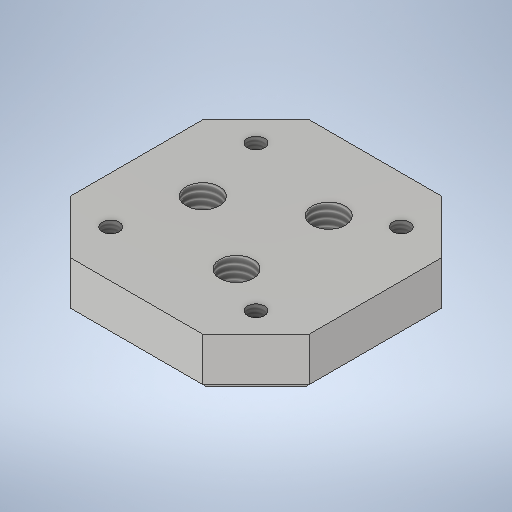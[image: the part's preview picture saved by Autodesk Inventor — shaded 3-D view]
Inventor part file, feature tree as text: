
AUTODESK INVENTOR PART (.ipt)
format: ipt  version: 2025 (Build 290162000, 162)  size: 306,176 bytes
history: native  units: in
note: dims shown in document units (in); Inventor stores cm internally (conversion verified against a paired STEP export)
features: sketch x3, hole x2, chamfer x2, extrude x1
ambient origin geometry x8: Origin, YZ Plane, XZ Plane, XY Plane, X Axis, Y Axis, Z Axis, Center Point
bodies: Solid1 (feature_tree)
feature tree (8):
  extrude  "Extrusion1"  Depth=1.122in
  hole  "Hole5"  [1 undecoded]
  chamfer  "Chamfer3"  Distance=0.25in
  chamfer  "Chamfer4"  Distance=0.25in Angle=45.0deg
  sketch  "Sketch Circular Pattern1"  dims[d0=1.122in d1=1.122in]
  sketch  "Sketch Circular Pattern2"  dims[d2=0.2362in d3=0.0in d55=0.1969in]
  sketch  "Sketch7"  dims[d65=0.8108in d66=0.5635in d67=0.25in d68=0.375in d69=0.2992in d70=0.0793in d77=0.25in d78=0.156in d79=0.38in d80=0.375in d81=0.19in d82=0.5635in d83=1.0in d84=0.8108in d85=0.25in d86=0.125in d87=45.0deg d88=0.0312in d89=0.125in d90=45.0deg d91=1.1811in d93=360.0deg d95=0.9646in d96=45.0deg d97=1.122in d98=1.122in d99=0.561in d100=0.561in d101=1.5748in d103=360.0deg]
  hole  "Hole4"  [1 undecoded]
note: 2 required parameter values undecoded (feature->parameter linkage not recoverable at this tier; creation-order binding heuristic only, values carry confidence <= 0.55)
